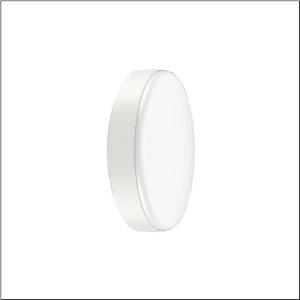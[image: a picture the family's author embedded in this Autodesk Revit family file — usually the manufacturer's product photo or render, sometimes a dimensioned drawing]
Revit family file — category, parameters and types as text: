
# Revit family: round_31_51wc10mb44a
name_source: partatom
category: Lighting Fixtures
units: mm (PartAtom-declared; Revit-internal decimal feet)

## family parameters
Cut with Voids When Loaded = No
Host = Face
Light Source = No
Part Type = Normal
Room Calculation Point = No
Round Connector Dimension = Use Diameter
Shared = No

## types (1)
- --- (1 x LED, 4400 lm, 34 W, 4000K)
    Apparent Load = 34 VA
    CIE Flux Codes = 44 75 94 94 100
    Color Rendering = 80
    Color Temperature = 4000K
    Default Elevation = 1800 mm
    Description = Round 31, wall and ceiling luminaire, primary optical cover: cover, of PC, opal, light emission: direct distribution, primary light characteristic: symmetric, installation type: surface-mounted, LED, rated luminous flux: 4.400lm, luminous efficacy: 129lm/W, light colour: 840, colour temperature: 4000K, control gear: ON/OFF Multilumen, with terminal, 3-pole, max. 2.5mm², mains connection: 220..240V, AC, 50/60Hz, rated input power: 34W, luminaire housing, of PC, traffic white (RAL 9016), diameter: 480mm, protection rating (complete): IP65, insulation class (complete): insulation class II (safety insulation), certification: CE, impact resistance: IK10, permissible operating ambient temperature: -20..+40°C, permissible storage temperature: -20..+60°C, packaging unit: 1 piece
    Height = 97 mm
    Lamp = 1 x LED
    Lamp Light Flux = 4400 lm
    Lamp Power = 34 W
    Lamp count = 1
    Length = 480 mm
    Luminous efficacy = 129 lm/W
    Manufacturer = Siteco
    ModVariant = No
    Model = 51WC10MB44A
    Mounting Place = Wall
    Mounting Type = Surface mounted
    Number of Poles = 1
    OnlyDefault = Yes
    Power Factor = 1
    Product Name = Round 31
    Product group = wall and ceiling luminaire
    ProductGroupID = 2001
    Protection Class = Protection class II
    Protection Degree = IP 65
    RLX_Detail_Level = 1
    RLX_Emergency_Light_Flux = 0 lm
    RLX_Emergency_Type = 0
    RLX_Emergency_Type_DB = No
    RlxData = <blob elided: 56365 chars, md5=7da5a886>
    Socket = socket
    Standby Power = 0 W
    System Light Flux = 4400 lm
    System Power = 34 W
    Type Comments = factory setting: luminous flux: 100 % | (ON | ON)
    Type Image = l_1007188.jpg
    URL = http://relux.com
    VarID = @adj_154083
    Voltage = 0 V
    Weight = 0.00 kg
    Width = 0 mm  [stored 0 ft]

note: [stored X ft] marks values corroborated as IEEE doubles in the binary element streams (Revit-internal decimal feet)

## geometry (parser evidence)
native form markers: Blend x4, Sweep x13
no freeform markers — native parametric forms only
